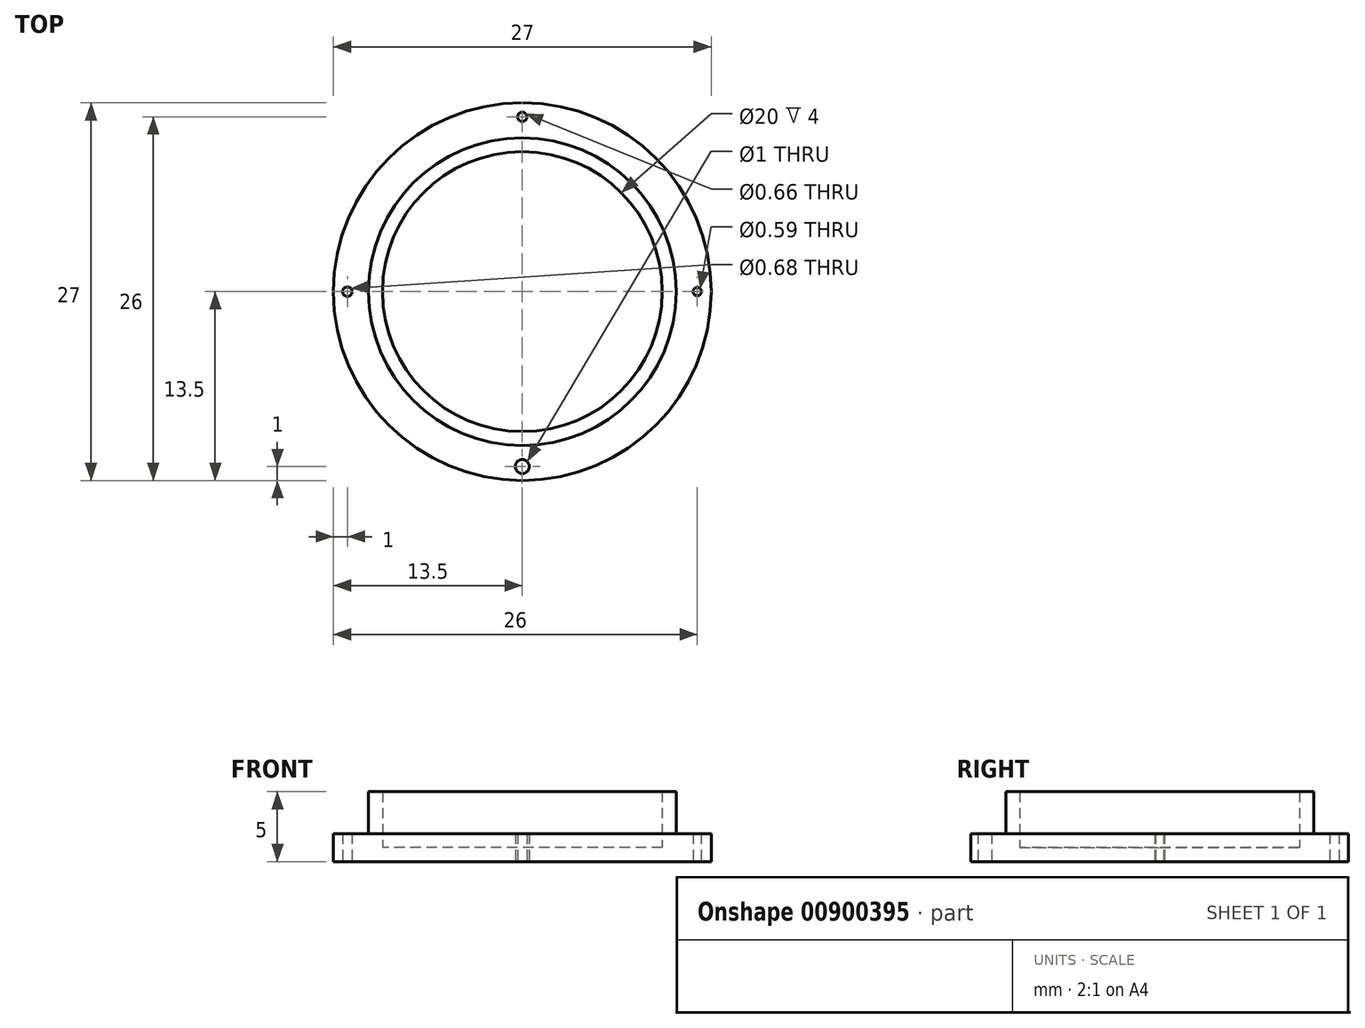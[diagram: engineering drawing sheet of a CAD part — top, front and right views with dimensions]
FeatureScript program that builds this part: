
annotation { "Feature Type Name" : "Feature", "Feature Type Description" : "" }
export const myFeature = defineFeature(function(context is Context, id is Id, definition is map)
    precondition{}
    {
        {
            var Q0;
            Q0=qCreatedBy(makeId("Top.planeOp"),FACE);
            var sketch = newSketch(context, id + "F0", { "sketchPlane" : qUnion([Q0])});
            skCircle(sketch, "E0", {"center": v(0, 0) * mm, "radius": 13.5 * mm});
            skCircle(sketch, "E1", {"center": v(0, 0) * mm, "radius": 11 * mm});
            skSolve(sketch);
        }
        {
            var Q0;
            Q0=makeQuery(id+"F0.imprint","IMPRINT",FACE,{"disambiguationData":[TD([[makeQuery(id+"F0.imprint","IMPRINT",EDGE,{"derivedFrom":sQuery(id+"F0.wireOp",EDGE,"E1")}),1.0]])]});
            extrude(context, id + "F1", {"entities" : qUnion([Q0]), "depth" : 5 * mm, "offsetDistance" : 25 * mm});
        }
        {
            var Q0;
            Q0=makeQuery(id+"F0.imprint","IMPRINT",FACE,{"disambiguationData":[TD([[makeQuery(id+"F0.imprint","IMPRINT",EDGE,{"derivedFrom":sQuery(id+"F0.wireOp",EDGE,"E0")}),1.0]])]});
            extrude(context, id + "F2", {"entities" : qUnion([Q0]), "operationType" : NewBodyOperationType.ADD, "depth" : 2 * mm, "offsetDistance" : 25 * mm});
        }
        {
            var Q0;
            Q0=makeQuery(id+"F1.opExtrude","CAP_FACE",FACE,{"disambiguationData":[OSD([sQuery(id+"F0.wireOp",EDGE,"E1")])],"isStart":false});
            shell(context, id + "F3", {"entities" : qUnion([Q0]), "thickness" : 1 * mm});
        }
        {
            var Q0;
            Q0=makeQuery(id+"F0.imprint","IMPRINT",FACE,{"disambiguationData":[TD([[makeQuery(id+"F0.imprint","IMPRINT",EDGE,{"derivedFrom":sQuery(id+"F0.wireOp",EDGE,"E0")}),1.0]])]});
            var sketch = newSketch(context, id + "F4", { "sketchPlane" : qUnion([Q0])});
            skCircle(sketch, "E2", {"center": v(-12.5, 0) * mm, "radius": 0.34 * mm});
            skCircle(sketch, "E3", {"center": v(12.5, 0) * mm, "radius": 0.3 * mm});
            skCircle(sketch, "E4", {"center": v(0, 12.5) * mm, "radius": 0.33 * mm});
            skCircle(sketch, "E5", {"center": v(0, -12.5) * mm, "radius": 0.5 * mm});
            skSolve(sketch);
        }
        {
            var Q0;
            Q0 = qSketchRegion(id + "F4", true);
            extrude(context, id + "F5", {"entities" : qUnion([Q0]), "operationType" : NewBodyOperationType.REMOVE, "endBound" : BoundingType.SYMMETRIC, "depth" : 253.6 * mm, "offsetDistance" : 25 * mm});
        }
    });
